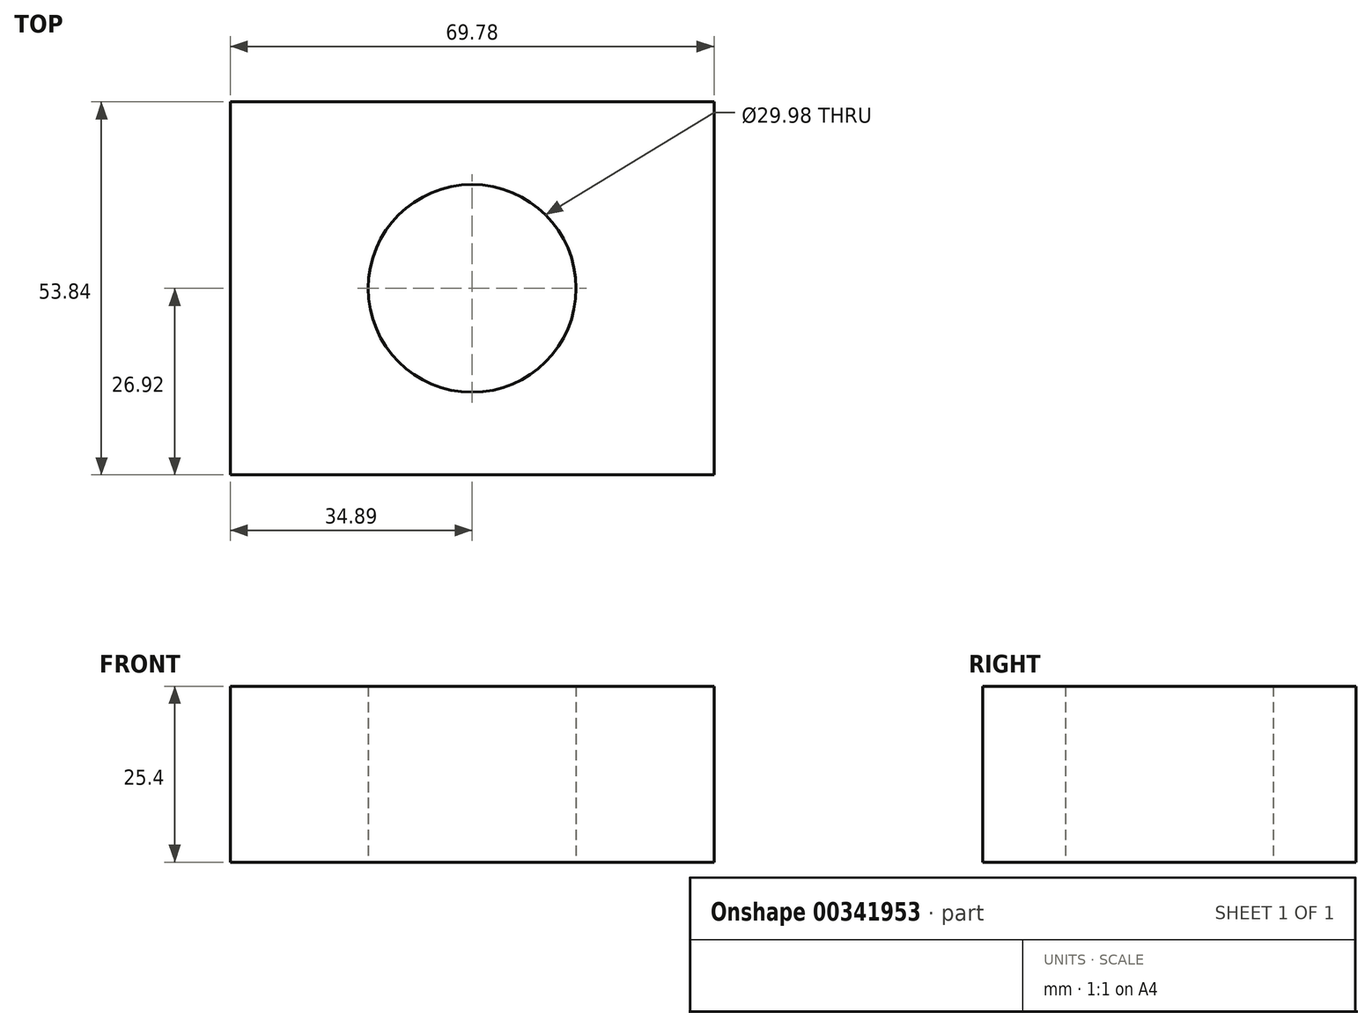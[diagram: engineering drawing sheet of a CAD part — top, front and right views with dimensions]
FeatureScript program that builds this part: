
annotation { "Feature Type Name" : "Feature", "Feature Type Description" : "" }
export const myFeature = defineFeature(function(context is Context, id is Id, definition is map)
    precondition{}
    {
        {
            var Q0;
            Q0=qCreatedBy(makeId("Top.planeOp"),FACE);
            var sketch = newSketch(context, id + "F0", { "sketchPlane" : qUnion([Q0])});
            skLineSegment(sketch, "E0.bottom", {"start": v(34.9, 26.92) * mm, "end": v(-34.9, 26.92) * mm});
            skLineSegment(sketch, "E0.top", {"start": v(34.9, -26.92) * mm, "end": v(-34.9, -26.92) * mm});
            skLineSegment(sketch, "E0.left", {"start": v(34.9, 26.92) * mm, "end": v(34.9, -26.92) * mm});
            skLineSegment(sketch, "E0.right", {"start": v(-34.9, 26.92) * mm, "end": v(-34.9, -26.92) * mm});
            skPoint(sketch, "E0.middle", {"position": v(0, 0) * mm});
            skCircle(sketch, "E1", {"center": v(0, 0) * mm, "radius": 15 * mm});
            skSolve(sketch);
        }
        {
            var Q0;
            Q0=makeQuery(id+"F0.imprint","IMPRINT",FACE,{"disambiguationData":[TD([[makeQuery(id+"F0.imprint","IMPRINT",EDGE,{"derivedFrom":sQuery(id+"F0.wireOp",EDGE,"E0.bottom")}),1.0]])]});
            extrude(context, id + "F1", {"entities" : qUnion([Q0]), "depth" : 25.4 * mm});
        }
    });
